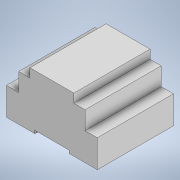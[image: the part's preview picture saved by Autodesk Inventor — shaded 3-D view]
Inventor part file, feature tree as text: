
AUTODESK INVENTOR PART (.ipt)
format: ipt  version: 2020 (Build 240168000, 168)  size: 132,608 bytes
history: native  units: mm
features: extrude x4, sketch x4
ambient origin geometry x8: Origin, YZ Plane, XZ Plane, XY Plane, X Axis, Y Axis, Z Axis, Center Point
bodies: Solid1 (feature_tree)
feature tree (8):
  extrude  "Extrusion1"  Depth=93.0mm
  extrude  "Extrusion2"  Depth=29.0mm
  extrude  "Extrusion3"  Depth=3.0mm TaperAngle=0.0deg
  extrude  "Extrusion4"  Depth=12.5mm
  sketch  "Sketch1"  dims[d0=78.0mm d1=93.0mm]
  sketch  "Sketch2"  dims[d2=56.0mm d3=0.0mm d4=29.0mm]
  sketch  "Sketch3"  dims[d5=35.0mm d6=3.0mm d7=0.0mm]
  sketch  "Sketch4"  dims[d8=12.5mm d9=12.5mm d10=27.6mm d11=0.0mm d12=11.5mm d13=11.5mm d14=9.0mm d15=0.0mm]
